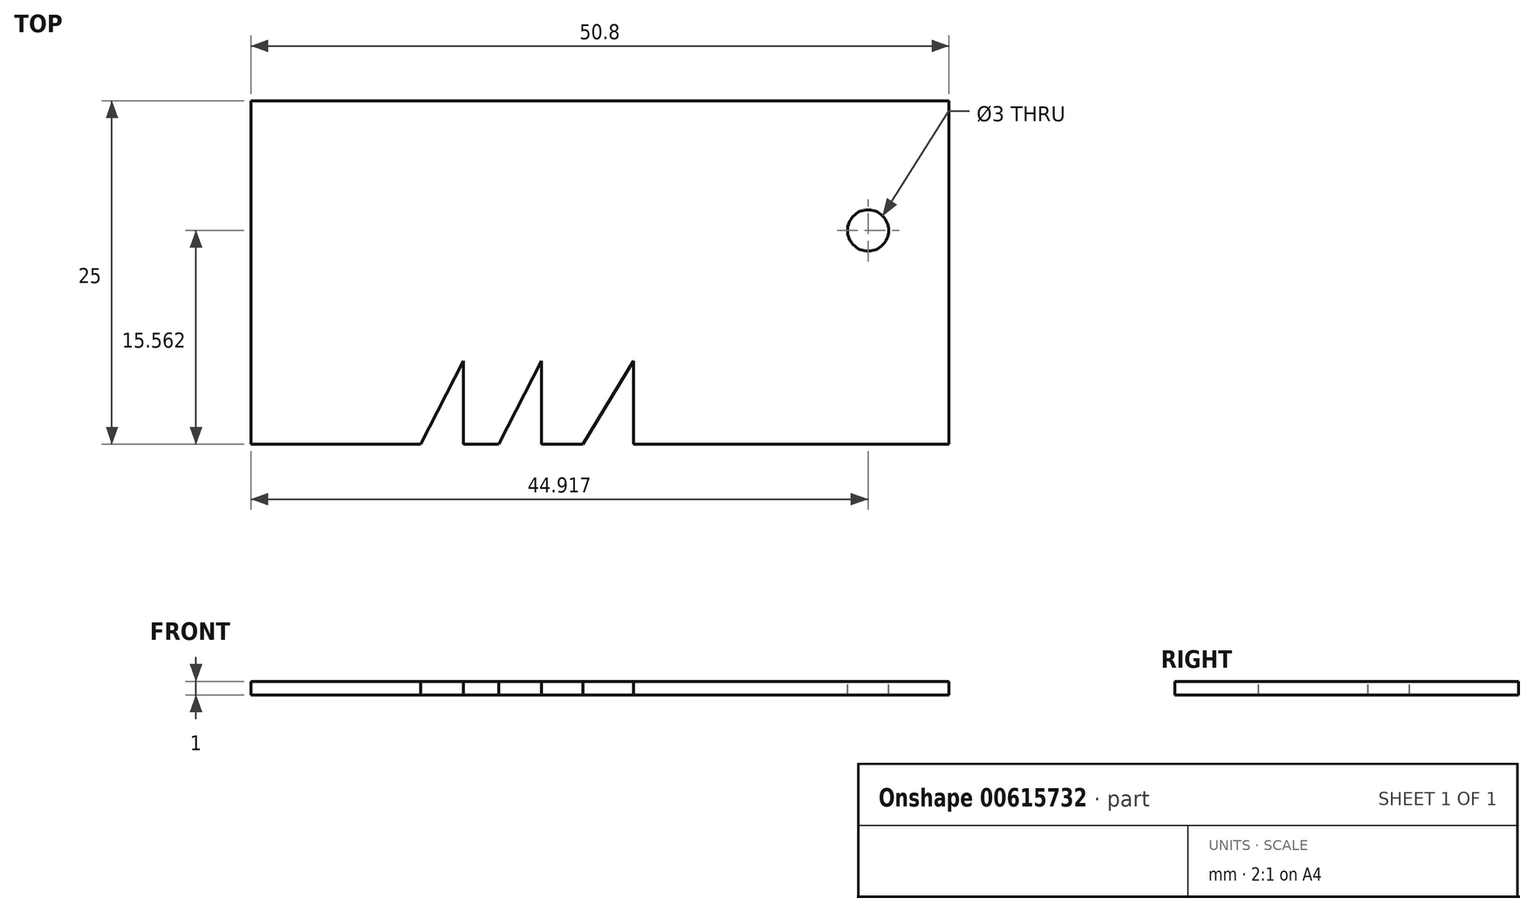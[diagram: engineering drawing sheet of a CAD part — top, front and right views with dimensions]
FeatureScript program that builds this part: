
annotation { "Feature Type Name" : "Feature", "Feature Type Description" : "" }
export const myFeature = defineFeature(function(context is Context, id is Id, definition is map)
    precondition{}
    {
        {
            var Q0;
            Q0=qCreatedBy(makeId("Top.planeOp"),FACE);
            var sketch = newSketch(context, id + "F0", { "sketchPlane" : qUnion([Q0])});
            skLineSegment(sketch, "E0.bottom", {"start": v(25.4, 12.5) * mm, "end": v(-25.4, 12.5) * mm});
            skLineSegment(sketch, "E0.top", {"start": v(25.4, -12.5) * mm, "end": v(-25.4, -12.5) * mm});
            skLineSegment(sketch, "E0.left", {"start": v(25.4, 12.5) * mm, "end": v(25.4, -12.5) * mm});
            skLineSegment(sketch, "E0.right", {"start": v(-25.4, 12.5) * mm, "end": v(-25.4, -12.5) * mm});
            skPoint(sketch, "E0.middle", {"position": v(0, 0) * mm});
            skSolve(sketch);
        }
        {
            var Q0;
            Q0=qSketchRegion(id+"F0",true);
            extrude(context, id + "F1", {"entities" : qUnion([Q0]), "depth" : 1 * mm, "offsetDistance" : 25 * mm});
        }
        {
            var Q0;
            Q0=makeQuery(id+"F1.opExtrude","CAP_FACE",FACE,{"disambiguationData":[OSD([sQuery(id+"F0.wireOp",EDGE,"E0.bottom"),sQuery(id+"F0.wireOp",EDGE,"E0.top"),sQuery(id+"F0.wireOp",EDGE,"E0.left"),sQuery(id+"F0.wireOp",EDGE,"E0.right")])],"isStart":false});
            var sketch = newSketch(context, id + "F2", { "sketchPlane" : qUnion([Q0])});
            skCircle(sketch, "E1", {"center": v(19.52, 3.06) * mm, "radius": 1.5 * mm});
            skSolve(sketch);
        }
        {
            var Q0;
            Q0=qSketchRegion(id+"F2",true);
            extrude(context, id + "F3", {"entities" : qUnion([Q0]), "operationType" : NewBodyOperationType.REMOVE, "oppositeDirection" : true, "depth" : 25 * mm, "offsetDistance" : 25 * mm});
        }
        {
            var Q0;
            Q0=makeQuery(id+"F1.opExtrude","CAP_FACE",FACE,{"disambiguationData":[OSD([sQuery(id+"F0.wireOp",EDGE,"E0.bottom"),sQuery(id+"F0.wireOp",EDGE,"E0.top"),sQuery(id+"F0.wireOp",EDGE,"E0.left"),sQuery(id+"F0.wireOp",EDGE,"E0.right")])],"isStart":false});
            var sketch = newSketch(context, id + "F4", { "sketchPlane" : qUnion([Q0])});
            skLineSegment(sketch, "E2", {"start": v(-13.04, -12.5) * mm, "end": v(-9.93, -6.41) * mm});
            skLineSegment(sketch, "E3", {"start": v(-9.93, -12.5) * mm, "end": v(-9.93, -6.41) * mm});
            skLineSegment(sketch, "E4", {"start": v(-7.37, -12.5) * mm, "end": v(-4.25, -6.41) * mm});
            skLineSegment(sketch, "E5", {"start": v(-4.25, -6.41) * mm, "end": v(-4.25, -12.5) * mm});
            skLineSegment(sketch, "E6", {"start": v(2.44, -6.41) * mm, "end": v(-1.25, -12.5) * mm});
            skLineSegment(sketch, "E7", {"start": v(2.44, -6.41) * mm, "end": v(2.44, -12.5) * mm});
            skSolve(sketch);
        }
        {
            var Q0;
            Q0=qSketchRegion(id+"F4",true);
            var Q1;
            {var subQ0=sQuery(id+"F4.wireOp",EDGE,"E4");Q1=makeQuery(id+"F4.imprint","IMPRINT",FACE,{"disambiguationData":[TD([[makeQuery(id+"F4.imprint","IMPRINT",EDGE,{"derivedFrom":subQ0}),-1.0]])]});}
            var Q2;
            {var subQ0=sQuery(id+"F4.wireOp",EDGE,"E6");Q2=makeQuery(id+"F4.imprint","IMPRINT",FACE,{"disambiguationData":[TD([[makeQuery(id+"F4.imprint","IMPRINT",EDGE,{"derivedFrom":subQ0}),1.0]])]});}
            var Q3;
            {var subQ0=sQuery(id+"F4.wireOp",EDGE,"E2");Q3=makeQuery(id+"F4.imprint","IMPRINT",FACE,{"disambiguationData":[TD([[makeQuery(id+"F4.imprint","IMPRINT",EDGE,{"derivedFrom":subQ0}),-1.0]])]});}
            extrude(context, id + "F5", {"entities" : qUnion([Q0, Q1, Q2, Q3]), "operationType" : NewBodyOperationType.REMOVE, "oppositeDirection" : true, "depth" : 25 * mm, "offsetDistance" : 25 * mm});
        }
    });
